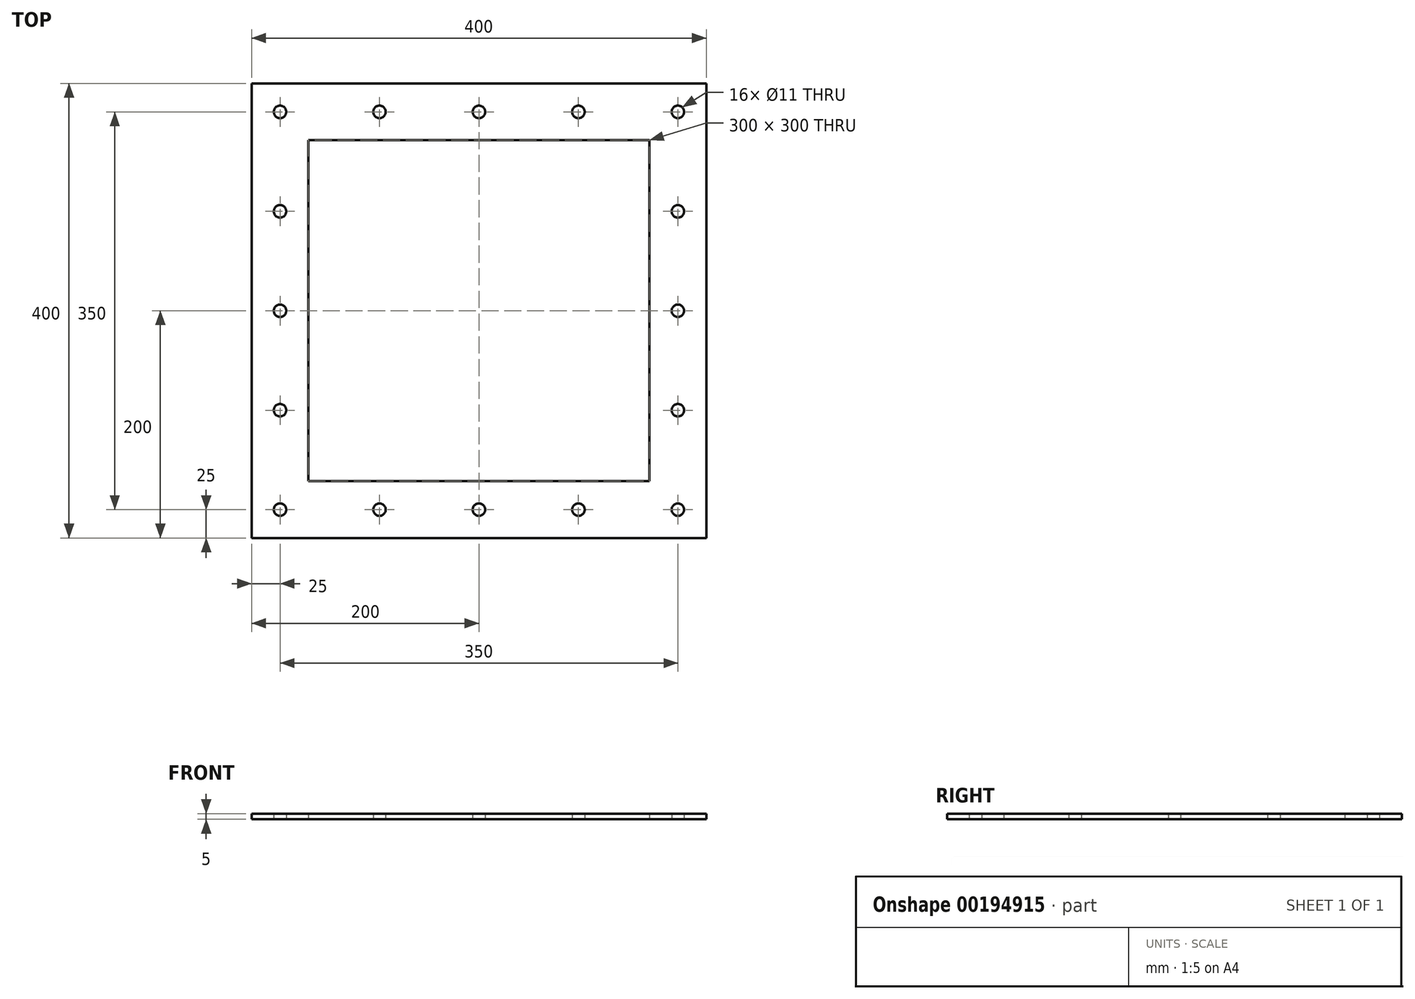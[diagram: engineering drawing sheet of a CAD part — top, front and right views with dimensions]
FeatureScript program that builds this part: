
annotation { "Feature Type Name" : "Feature", "Feature Type Description" : "" }
export const myFeature = defineFeature(function(context is Context, id is Id, definition is map)
    precondition{}
    {
        {
            var Q0;
            Q0=qCreatedBy(makeId("Top.planeOp"),FACE);
            var sketch = newSketch(context, id + "F0", { "sketchPlane" : qUnion([Q0])});
            skLineSegment(sketch, "E0.bottom", {"start": v(-200, -200) * mm, "end": v(200, -200) * mm});
            skLineSegment(sketch, "E0.top", {"start": v(-200, 200) * mm, "end": v(200, 200) * mm});
            skLineSegment(sketch, "E0.left", {"start": v(-200, -200) * mm, "end": v(-200, 200) * mm});
            skLineSegment(sketch, "E0.right", {"start": v(200, -200) * mm, "end": v(200, 200) * mm});
            skPoint(sketch, "E0.middle", {"position": v(0, 0) * mm});
            skLineSegment(sketch, "E1.bottom", {"start": v(150, 150) * mm, "end": v(-150, 150) * mm});
            skLineSegment(sketch, "E1.top", {"start": v(150, -150) * mm, "end": v(-150, -150) * mm});
            skLineSegment(sketch, "E1.left", {"start": v(150, 150) * mm, "end": v(150, -150) * mm});
            skLineSegment(sketch, "E1.right", {"start": v(-150, 150) * mm, "end": v(-150, -150) * mm});
            skCircle(sketch, "E2", {"center": v(0, 175) * mm, "radius": 5.5 * mm});
            skPoint(sketch, "E2.centerSnap0", {"position": v(0, 150) * mm});
            skCircle(sketch, "E3", {"center": v(175, 0) * mm, "radius": 5.5 * mm});
            skCircle(sketch, "E4", {"center": v(0, -175) * mm, "radius": 5.5 * mm});
            skCircle(sketch, "E5", {"center": v(-175, 0) * mm, "radius": 5.5 * mm});
            skPoint(sketch, "E5.centerSnap0", {"position": v(-150, 0) * mm});
            skCircle(sketch, "E6", {"center": v(87.5, 175) * mm, "radius": 5.5 * mm});
            skCircle(sketch, "E7", {"center": v(175, 87.5) * mm, "radius": 5.5 * mm});
            skCircle(sketch, "E8", {"center": v(175, -87.5) * mm, "radius": 5.5 * mm});
            skCircle(sketch, "E9", {"center": v(87.5, -175) * mm, "radius": 5.5 * mm});
            skCircle(sketch, "E10", {"center": v(175, -175) * mm, "radius": 5.5 * mm});
            skCircle(sketch, "E11", {"center": v(175, 175) * mm, "radius": 5.5 * mm});
            skCircle(sketch, "E12", {"center": v(-87.5, -175) * mm, "radius": 5.5 * mm});
            skCircle(sketch, "E13", {"center": v(-175, -175) * mm, "radius": 5.5 * mm});
            skCircle(sketch, "E14", {"center": v(-175, -87.5) * mm, "radius": 5.5 * mm});
            skCircle(sketch, "E15", {"center": v(-175, 87.5) * mm, "radius": 5.5 * mm});
            skCircle(sketch, "E16", {"center": v(-175, 175) * mm, "radius": 5.5 * mm});
            skCircle(sketch, "E17", {"center": v(-87.5, 175) * mm, "radius": 5.5 * mm});
            skSolve(sketch);
        }
        {
            var Q0;
            Q0 = qSketchRegion(id + "F0", true);
            extrude(context, id + "F1", {"entities" : qUnion([Q0]), "depth" : 5 * mm});
        }
    });
